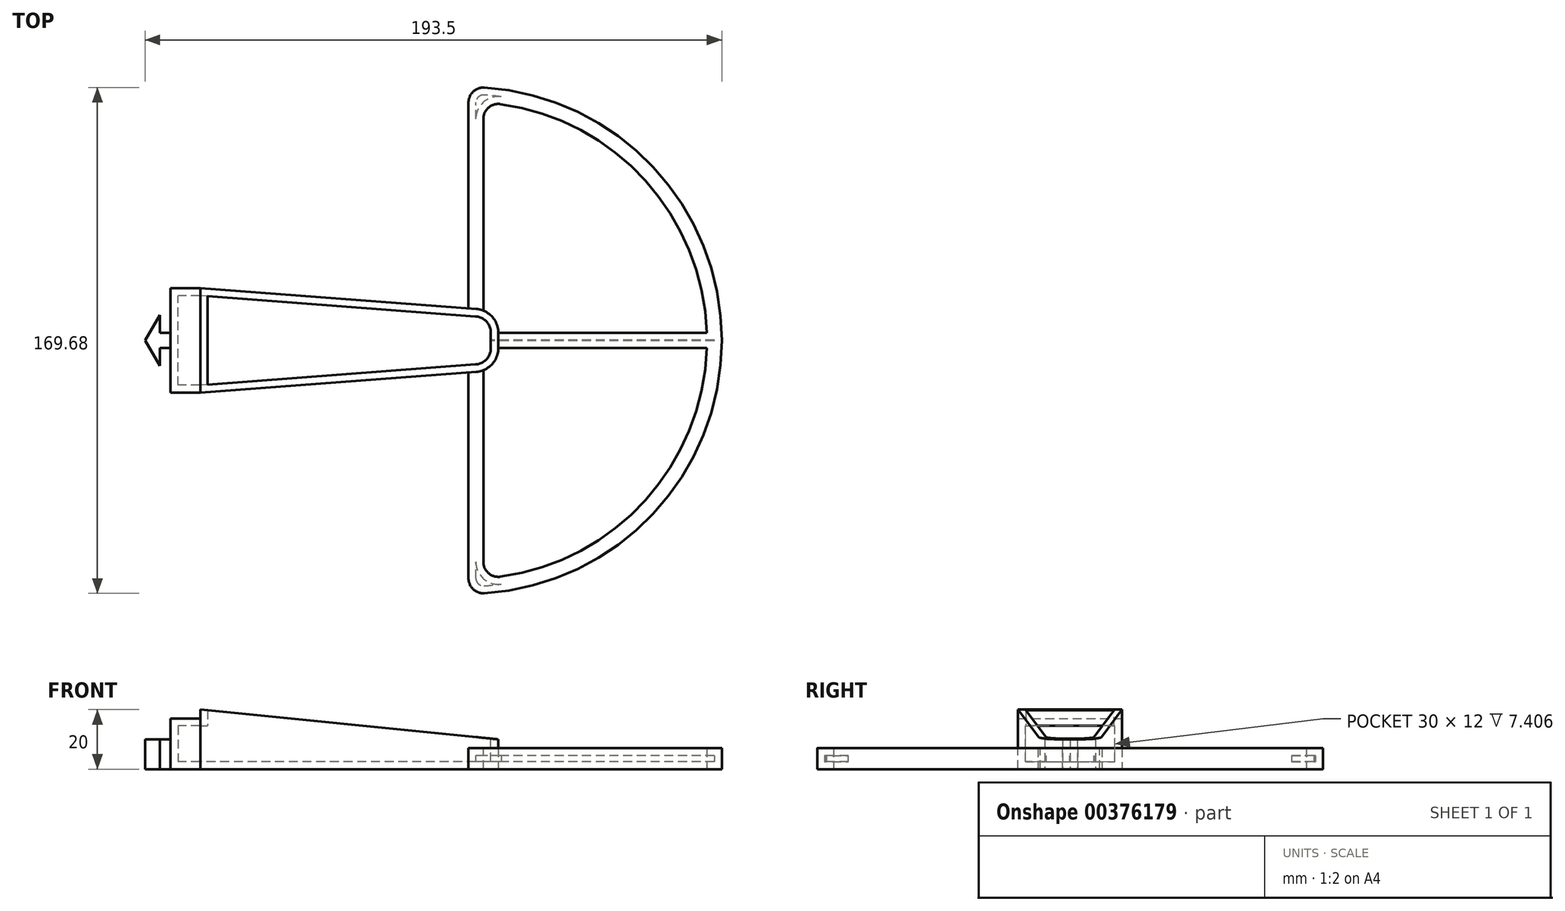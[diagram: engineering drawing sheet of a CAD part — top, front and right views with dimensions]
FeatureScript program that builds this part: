
annotation { "Feature Type Name" : "Feature", "Feature Type Description" : "" }
export const myFeature = defineFeature(function(context is Context, id is Id, definition is map)
    precondition{}
    {
        {
            var Q0;
            Q0=qCreatedBy(makeId("Top.planeOp"),FACE);
            var sketch = newSketch(context, id + "F0", { "sketchPlane" : qUnion([Q0])});
            skLineSegment(sketch, "E0.bottom", {"start": v(55, -17.5) * mm, "end": v(-55, -17.5) * mm});
            skLineSegment(sketch, "E0.top", {"start": v(55, 17.5) * mm, "end": v(-55, 17.5) * mm});
            skLineSegment(sketch, "E0.left", {"start": v(55, -17.5) * mm, "end": v(55, 17.5) * mm});
            skLineSegment(sketch, "E0.right", {"start": v(-55, -17.5) * mm, "end": v(-55, 17.5) * mm});
            skPoint(sketch, "E0.middle", {"position": v(0, 0) * mm});
            skLineSegment(sketch, "E1.bottom", {"start": v(-55, -2.5) * mm, "end": v(-58.5, -2.5) * mm});
            skLineSegment(sketch, "E1.top", {"start": v(-55, 2.5) * mm, "end": v(-58.5, 2.5) * mm});
            skLineSegment(sketch, "E1.left", {"start": v(-55, -2.5) * mm, "end": v(-55, 2.5) * mm});
            skLineSegment(sketch, "E1.right", {"start": v(-58.5, -2.5) * mm, "end": v(-58.5, 2.5) * mm});
            skPoint(sketch, "E1.middle", {"position": v(-56.75, 0) * mm});
            skPoint(sketch, "E2", {"position": v(-58.5, 8.5) * mm});
            skPoint(sketch, "E3", {"position": v(-58.5, -8.5) * mm});
            skPoint(sketch, "E4", {"position": v(-58.5, 0) * mm});
            skLineSegment(sketch, "E5", {"start": v(-58.5, 0) * mm, "end": v(-58.5, 8.5) * mm});
            skLineSegment(sketch, "E6", {"start": v(-58.5, 0) * mm, "end": v(-58.5, -8.5) * mm});
            skPoint(sketch, "E7", {"position": v(-63.5, 0) * mm});
            skLineSegment(sketch, "E8", {"start": v(-58.5, 8.5) * mm, "end": v(-63.5, 0) * mm});
            skLineSegment(sketch, "E9", {"start": v(-58.5, -8.5) * mm, "end": v(-63.5, 0) * mm});
            skSolve(sketch);
        }
        {
            var Q0;
            {var subQ6=sQuery(id+"F0.wireOp",EDGE,"E8");Q0=makeQuery(id+"F0.imprint","IMPRINT",FACE,{"disambiguationData":[TD([[makeQuery(id+"F0.imprint","IMPRINT",EDGE,{"derivedFrom":subQ6}),1.0]])]});}
            var Q1;
            {var subQ4=sQuery(id+"F0.wireOp",EDGE,"E1.bottom");Q1=makeQuery(id+"F0.imprint","IMPRINT",FACE,{"disambiguationData":[TD([[makeQuery(id+"F0.imprint","IMPRINT",EDGE,{"derivedFrom":subQ4}),-1.0]])]});}
            extrude(context, id + "F1", {"entities" : qUnion([Q0, Q1]), "depth" : 10 * mm});
        }
        {
            var Q0;
            {var subQ1=sQuery(id+"F0.wireOp",EDGE,"E0.bottom");Q0=makeQuery(id+"F0.imprint","IMPRINT",FACE,{"disambiguationData":[TD([[makeQuery(id+"F0.imprint","IMPRINT",EDGE,{"derivedFrom":subQ1}),-1.0]])]});}
            extrude(context, id + "F2", {"entities" : qUnion([Q0]), "operationType" : NewBodyOperationType.ADD, "depth" : 17 * mm});
        }
        {
            var Q0;
            Q0=makeQuery(id+"F2.opExtrude","CAP_FACE",FACE,{"disambiguationData":[OSD([sQuery(id+"F0.wireOp",EDGE,"E0.bottom"),sQuery(id+"F0.wireOp",EDGE,"E0.top"),sQuery(id+"F0.wireOp",EDGE,"E0.left"),sQuery(id+"F0.wireOp",EDGE,"E0.right"),sQuery(id+"F0.wireOp",EDGE,"E1.left")])],"isStart":false});
            var sketch = newSketch(context, id + "F3", { "sketchPlane" : qUnion([Q0])});
            skLineSegment(sketch, "E10.bottom", {"start": v(55, 17.5) * mm, "end": v(-45, 17.5) * mm});
            skLineSegment(sketch, "E10.top", {"start": v(55, -17.5) * mm, "end": v(-45, -17.5) * mm});
            skLineSegment(sketch, "E10.left", {"start": v(55, 17.5) * mm, "end": v(55, -17.5) * mm});
            skLineSegment(sketch, "E10.right", {"start": v(-45, 17.5) * mm, "end": v(-45, -17.5) * mm});
            skSolve(sketch);
        }
        {
            var Q0;
            Q0=makeQuery(id+"F3.imprint","IMPRINT",FACE,{"disambiguationData":[TD([[makeQuery(id+"F3.imprint","IMPRINT",EDGE,{"derivedFrom":sQuery(id+"F3.wireOp",EDGE,"E10.bottom")}),1.0]])]});
            extrude(context, id + "F4", {"entities" : qUnion([Q0]), "operationType" : NewBodyOperationType.ADD, "depth" : 3 * mm});
        }
        {
            var Q0;
            Q0=makeQuery(id+"F4.boolean.opBoolean","MERGE",EDGE,{"derivedFrom":[makeQuery(id+"F2.opExtrude","SWEPT_EDGE",EDGE,{"disambiguationData":[OSD([sQuery(id+"F0.wireOp",EDGE,"E0.bottom"),sQuery(id+"F0.wireOp",EDGE,"E0.left")])]}),makeQuery(id+"F4.opExtrude","SWEPT_EDGE",EDGE,{"disambiguationData":[OSD([sQuery(id+"F3.wireOp",EDGE,"E10.top"),sQuery(id+"F3.wireOp",EDGE,"E10.left")])]})]});
            var Q1;
            Q1=makeQuery(id+"F4.boolean.opBoolean","MERGE",EDGE,{"derivedFrom":[makeQuery(id+"F2.opExtrude","SWEPT_EDGE",EDGE,{"disambiguationData":[OSD([sQuery(id+"F0.wireOp",EDGE,"E0.top"),sQuery(id+"F0.wireOp",EDGE,"E0.left")])]}),makeQuery(id+"F4.opExtrude","SWEPT_EDGE",EDGE,{"disambiguationData":[OSD([sQuery(id+"F3.wireOp",EDGE,"E10.bottom"),sQuery(id+"F3.wireOp",EDGE,"E10.left")])]})]});
            chamfer(context, id + "F5", {"entities" : qUnion([Q0, Q1]), "chamferType" : ChamferType.TWO_OFFSETS, "width1" : 7.5 * mm, "oppositeDirection" : false, "width2" : 100 * mm, "tangentPropagation" : true});
        }
        {
            var Q0;
            Q0=makeQuery(id+"F4.opExtrude","CAP_EDGE",EDGE,{"disambiguationData":[OSD([sQuery(id+"F3.wireOp",EDGE,"E10.left")])],"isStart":false});
            chamfer(context, id + "F6", {"entities" : qUnion([Q0]), "chamferType" : ChamferType.TWO_OFFSETS, "width1" : 100 * mm, "oppositeDirection" : false, "width2" : 10 * mm, "tangentPropagation" : true});
        }
        {
            var Q0;
            {var subQ0=sQuery(id+"F3.wireOp",EDGE,"E10.left");var subQ1=sQuery(id+"F0.wireOp",EDGE,"E0.left");Q0=makeQuery(id+"F5.opChamfer","BLEND_EDGE",EDGE,{"blendedFrom":[makeQuery(id+"F4.boolean.opBoolean","MERGE",EDGE,{"derivedFrom":[makeQuery(id+"F2.opExtrude","SWEPT_EDGE",EDGE,{"disambiguationData":[OSD([sQuery(id+"F0.wireOp",EDGE,"E0.bottom"),subQ1])]}),makeQuery(id+"F4.opExtrude","SWEPT_EDGE",EDGE,{"disambiguationData":[OSD([sQuery(id+"F3.wireOp",EDGE,"E10.top"),subQ0])]})]}),makeQuery(id+"F4.boolean.opBoolean","MERGE",FACE,{"derivedFrom":[makeQuery(id+"F2.opExtrude","SWEPT_FACE",FACE,{"disambiguationData":[OSD([subQ1])]}),makeQuery(id+"F4.opExtrude","SWEPT_FACE",FACE,{"disambiguationData":[OSD([subQ0])]})]})],"blendedInto":[makeQuery(id+"F4.boolean.opBoolean","MERGE",FACE,{"derivedFrom":[makeQuery(id+"F2.opExtrude","SWEPT_FACE",FACE,{"disambiguationData":[OSD([subQ1])]}),makeQuery(id+"F4.opExtrude","SWEPT_FACE",FACE,{"disambiguationData":[OSD([subQ0])]})]})]});}
            var Q1;
            {var subQ0=sQuery(id+"F3.wireOp",EDGE,"E10.left");var subQ1=sQuery(id+"F0.wireOp",EDGE,"E0.left");Q1=makeQuery(id+"F5.opChamfer","BLEND_EDGE",EDGE,{"blendedFrom":[makeQuery(id+"F4.boolean.opBoolean","MERGE",EDGE,{"derivedFrom":[makeQuery(id+"F2.opExtrude","SWEPT_EDGE",EDGE,{"disambiguationData":[OSD([sQuery(id+"F0.wireOp",EDGE,"E0.top"),subQ1])]}),makeQuery(id+"F4.opExtrude","SWEPT_EDGE",EDGE,{"disambiguationData":[OSD([sQuery(id+"F3.wireOp",EDGE,"E10.bottom"),subQ0])]})]}),makeQuery(id+"F4.boolean.opBoolean","MERGE",FACE,{"derivedFrom":[makeQuery(id+"F2.opExtrude","SWEPT_FACE",FACE,{"disambiguationData":[OSD([subQ1])]}),makeQuery(id+"F4.opExtrude","SWEPT_FACE",FACE,{"disambiguationData":[OSD([subQ0])]})]})],"blendedInto":[makeQuery(id+"F4.boolean.opBoolean","MERGE",FACE,{"derivedFrom":[makeQuery(id+"F2.opExtrude","SWEPT_FACE",FACE,{"disambiguationData":[OSD([subQ1])]}),makeQuery(id+"F4.opExtrude","SWEPT_FACE",FACE,{"disambiguationData":[OSD([subQ0])]})]})]});}
            fillet(context, id + "F7", {"entities" : qUnion([Q0, Q1]), "radius" : 8 * mm, "tangentPropagation" : true, "allowEdgeOverflow" : false});
        }
        {
            var Q0;
            {var subQ1=sQuery(id+"F0.wireOp",EDGE,"E0.bottom");Q0=makeQuery(id+"F0.imprint","IMPRINT",FACE,{"disambiguationData":[TD([[makeQuery(id+"F0.imprint","IMPRINT",EDGE,{"derivedFrom":subQ1}),-1.0]])]});}
            var sketch = newSketch(context, id + "F8", { "sketchPlane" : qUnion([Q0])});
            skPoint(sketch, "E11", {"position": v(45, 0) * mm});
            skArc(sketch, "E12", {"start": v(50.31, 84.83) * mm, "mid": v(130, 0) * mm, "end": v(50.31, -84.83) * mm});
            skLineSegment(sketch, "E13", {"start": v(45, -79.84) * mm, "end": v(45, 79.84) * mm});
            skLineSegment(sketch, "E14", {"start": v(45, 0) * mm, "end": v(118.61, -42.5) * mm});
            skLineSegment(sketch, "E15", {"start": v(45, 0) * mm, "end": v(118.61, 42.5) * mm});
            skArc(sketch, "E16.0", {"start": v(55.67, 79.29) * mm, "mid": v(125, 0) * mm, "end": v(55.67, -79.29) * mm});
            skLineSegment(sketch, "E16.1", {"start": v(50, -74.33) * mm, "end": v(50, 74.33) * mm});
            skLineSegment(sketch, "E17.0", {"start": v(55, 0) * mm, "end": v(121.11, 38.17) * mm});
            skLineSegment(sketch, "E17.1", {"start": v(55, 0) * mm, "end": v(121.11, -38.17) * mm});
            skPoint(sketch, "E18.visualSharp", {"position": v(45, -85) * mm});
            skArc(sketch, "E18.filletArc", {"start": v(45, -79.84) * mm, "mid": v(46.58, -83.49) * mm, "end": v(50.31, -84.83) * mm});
            skPoint(sketch, "E19.visualSharp", {"position": v(45, 85) * mm});
            skArc(sketch, "E19.filletArc", {"start": v(50.31, 84.83) * mm, "mid": v(46.58, 83.49) * mm, "end": v(45, 79.84) * mm});
            skArc(sketch, "E20.filletArc", {"start": v(50, -74.33) * mm, "mid": v(51.7, -78.1) * mm, "end": v(55.67, -79.29) * mm});
            skArc(sketch, "E21.filletArc", {"start": v(55.67, 79.29) * mm, "mid": v(51.7, 78.1) * mm, "end": v(50, 74.33) * mm});
            skSolve(sketch);
        }
        {
            var Q0;
            Q0=qSketchRegion(id+"F8",true);
            extrude(context, id + "F9", {"entities" : qUnion([Q0]), "operationType" : NewBodyOperationType.ADD, "depth" : 7 * mm});
        }
        {
            var Q0;
            Q0=makeQuery(id+"F4.boolean.opBoolean","MERGE",FACE,{"derivedFrom":[makeQuery(id+"F2.opExtrude","SWEPT_FACE",FACE,{"disambiguationData":[OSD([sQuery(id+"F0.wireOp",EDGE,"E0.left")])]}),makeQuery(id+"F4.opExtrude","SWEPT_FACE",FACE,{"disambiguationData":[OSD([sQuery(id+"F3.wireOp",EDGE,"E10.left")])]})]});
            var sketch = newSketch(context, id + "F10", { "sketchPlane" : qUnion([Q0])});
            skLineSegment(sketch, "E22.bottom", {"start": v(-2.58, 0) * mm, "end": v(2.58, 0) * mm});
            skLineSegment(sketch, "E22.top", {"start": v(-2.58, 7) * mm, "end": v(2.58, 7) * mm});
            skLineSegment(sketch, "E22.left", {"start": v(-2.58, 0) * mm, "end": v(-2.58, 7) * mm});
            skLineSegment(sketch, "E22.right", {"start": v(2.58, 0) * mm, "end": v(2.58, 7) * mm});
            skSolve(sketch);
        }
        {
            var Q0;
            Q0=makeQuery(id+"F10.imprint","IMPRINT",FACE,{"disambiguationData":[TD([[makeQuery(id+"F10.imprint","IMPRINT",EDGE,{"derivedFrom":sQuery(id+"F10.wireOp",EDGE,"E22.bottom")}),1.0]])]});
            extrude(context, id + "F11", {"entities" : qUnion([Q0]), "operationType" : NewBodyOperationType.ADD, "endBound" : BoundingType.UP_TO_NEXT, "depth" : 25 * mm});
        }
        {
            var Q0;
            Q0=makeQuery(id+"F6.opChamfer","BLEND_FACE",FACE,{"disambiguationData":[OSD([sQuery(id+"F3.wireOp",EDGE,"E10.left")])]});
            shell(context, id + "F12", {"entities" : qUnion([Q0]), "thickness" : 2.5 * mm});
        }
    });
